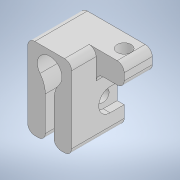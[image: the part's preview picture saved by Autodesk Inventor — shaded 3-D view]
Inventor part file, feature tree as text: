
AUTODESK INVENTOR PART (.ipt)
format: ipt  version: 2022 (Build 260153000, 153)  size: 221,184 bytes
history: native  units: in
note: dims shown in document units (in); Inventor stores cm internally (conversion verified against a paired STEP export)
features: sketch x4, extrude x4, hole x3, projected_geometry x2, plane x1, fillet x1
ambient origin geometry x8: Origin, YZ Plane, XZ Plane, XY Plane, X Axis, Y Axis, Z Axis, Center Point
bodies: Body1 (feature_tree)
feature tree (15):
  sketch  "Sketch14"  dims[d67=0.2756in d68=0.0984in]
  extrude  "Extrusion8"  Depth=0.0984in
  extrude  "Extrusion9"  Depth=0.2756in
  hole  "Hole12"  [1 undecoded]
  plane  "Work Plane4"
  sketch  "Sketch18"  dims[d69=0.2756in d70=0.2756in]
  extrude  "Extrusion13"  Depth=0.1969in
  hole  "Hole16"  [1 undecoded]
  hole  "Hole15"  [1 undecoded]
  extrude  "Extrusion14"  [1 undecoded]
  fillet  "Fillet3"  Radius=0.315in
  sketch  "Sketch19"  dims[d71=0.5906in d72=0.1969in]
  projected_geometry  "Projected Loop2"
  sketch  "Sketch20"  dims[d73=0.1969in d74=0.1969in d75=0.2756in d76=0.0in d77=0.315in d78=0.0in d79=0.1575in d80=0.2362in d81=0.1575in d82=0.0787in d83=90.0deg d84=0.315in d85=0.8108in d111=-0.1181in d112=0.315in d113=0.2165in d116=0.2362in d117=0.0in d126=0.1339in d127=0.2362in d128=0.2559in d129=0.0787in d130=90.0deg d131=0.315in d132=0.8108in d133=0.2362in d134=0.0in d135=0.0787in d139=0.315in d140=0.1575in d141=0.2362in d142=0.1575in d143=0.0787in d144=90.0deg d145=0.315in d146=0.8108in]
  projected_geometry  "Projected Loop3"
note: 4 required parameter values undecoded (feature->parameter linkage not recoverable at this tier; creation-order binding heuristic only, values carry confidence <= 0.55)
